# Revit family: Casement_38_B_Side_Hung_Standard
name_source: partatom
category: Windows
revit_build: Autodesk Revit 2014 (Build: 20130308_1515(x64)
units: mm (PartAtom-declared; Revit-internal decimal feet)

## types (18) — shared parameters
Aluminium Thickness = 1 mm  [stored 0.00328084 ft]
Bead SG Gap = 13 mm  [stored 0.0426509 ft]
Casement Dimension = 38 mm  [stored 0.124672 ft]
Custom Sash Width = 554 mm  [stored 1.81759 ft]
DG Extrusion Start = 9 mm  [stored 0.0295276 ft]
DG Gasket Finish = Double Glazing Gasket Material
DG Thickness Calc = 4 mm  [stored 0.0131234 ft]
Default Sill Height = 800 mm  [stored 2.62467 ft]
Depth Bead = 24 mm  [stored 0.0787402 ft]
Description = Window 38mm, Type B side hung
Frame Center Offset = 19 mm  [stored 0.062336 ft]
Limit Fixed Panel Width Max = 1500 mm
Limit Fixed Panel Width Min = 200 mm  [stored 0.656168 ft]
Limit Sash Height Max = 1500 mm
Limit Sash Height Min = 300 mm  [stored 0.984252 ft]
Limit Sash Width Max = 700 mm  [stored 2.29659 ft]
Limit Sash Width Min = 300 mm  [stored 0.984252 ft]
Limit Window Height Max = 1546 mm
Limit Window Height Min = 346 mm
Limit Window Width Max = 2129 mm
Limit Window Width Min = 829 mm  [stored 2.71982 ft]
Manufacturer = Crealco
Max System DG One Piece Thickness = 6 mm  [stored 0.019685 ft]
Max System DG Unit Thickness = 25 mm  [stored 0.082021 ft]
Model = Casement 38
Offset Bead SG Center Reversed = 19 mm  [stored 0.062336 ft]
Offset Mullion Left = 569 mm  [stored 1.8668 ft]
Offset Panel 4 Left = 599 mm  [stored 1.96522 ft]
Offset Sash Left = 23 mm  [stored 0.0754593 ft]
Offset Sash Top = 23 mm  [stored 0.0754593 ft]
Offset Window Exterior = 19 mm  [stored 0.062336 ft]
SG Gasket Thickness = 6 mm  [stored 0.019685 ft]
Sash Center Offset = 16 mm  [stored 0.0524934 ft]
Sash Overlap = 7 mm  [stored 0.0229659 ft]
Sash Spacing Inner = 8 mm  [stored 0.0262467 ft]
URL = http://www.crealco.co.za
Wall Closure = By host
Width Bead = 15 mm  [stored 0.0492126 ft]
Width Panel 1 = 539 mm  [stored 1.76837 ft]
Width Profile = 30 mm  [stored 0.0984252 ft]
Width Sash = 524 mm  [stored 1.71916 ft]
Width Sash Opening = 554 mm  [stored 1.81759 ft]
zero-valued in all types: Window Exterior Offset

## per-type parameters (varying)
- 38-0909S-1000Pa: Area Pane Left=0.37 m²; Area Pane Right=0.21 m²; Clearvue Insulated LowE SHGC Value=0.461; Clearvue Insulated LowE U Value=3.73; Clearvue Insulated SHGC Value=0.505; Clearvue Insulated U Value=4.2; Clearvue U Value=6.25; Custom Windload=1000 mm  [stored 3.28084 ft]; Custom Window Height=890 mm  [stored 2.91995 ft]; Custom Window Width=890 mm  [stored 2.91995 ft]; Depth Mullion=39 mm  [stored 0.127953 ft]; Energy Advantage SHGC Value=0.519; Energy Advantage U Value=4.82; Height=890 mm  [stored 2.91995 ft]; Height Panel 4=830 mm  [stored 2.7231 ft]; Height Sash=814 mm  [stored 2.6706 ft]; Height Sash Opening=844 mm  [stored 2.76903 ft]; Intruderprufe Insulated LowE SHGC Value=0.428; Intruderprufe Insulated LowE U Value=3.69; Intruderprufe Insulated SHGC Value=0.469; Intruderprufe Insulated U Value=4.1; Intruderprufe LowE SHGC Value=0.487; Intruderprufe LowE U Value=4.7; Intruderprufe SHGC Value=0.562; Intruderprufe U Value=6.12; Length Mullion=890 mm  [stored 2.91995 ft]; Max Pane Area=0.37 m²; Mullion Depth Windload Based=39 mm  [stored 0.127953 ft]; Width=890 mm  [stored 2.91995 ft]; Width Panel 4=261 mm  [stored 0.856299 ft]; Windload Design=1000 mm  [stored 3.28084 ft]
- 38-0909S-1500Pa: Area Pane Left=0.37 m²; Area Pane Right=0.21 m²; Clearvue Insulated LowE SHGC Value=0.461; Clearvue Insulated LowE U Value=3.73; Clearvue Insulated SHGC Value=0.505; Clearvue Insulated U Value=4.2; Clearvue U Value=6.25; Custom Windload=1500 mm; Custom Window Height=890 mm  [stored 2.91995 ft]; Custom Window Width=890 mm  [stored 2.91995 ft]; Depth Mullion=39 mm  [stored 0.127953 ft]; Energy Advantage SHGC Value=0.519; Energy Advantage U Value=4.82; Height=890 mm  [stored 2.91995 ft]; Height Panel 4=830 mm  [stored 2.7231 ft]; Height Sash=814 mm  [stored 2.6706 ft]; Height Sash Opening=844 mm  [stored 2.76903 ft]; Intruderprufe Insulated LowE SHGC Value=0.428; Intruderprufe Insulated LowE U Value=3.69; Intruderprufe Insulated SHGC Value=0.469; Intruderprufe Insulated U Value=4.1; Intruderprufe LowE SHGC Value=0.487; Intruderprufe LowE U Value=4.7; Intruderprufe SHGC Value=0.562; Intruderprufe U Value=6.12; Length Mullion=890 mm  [stored 2.91995 ft]; Max Pane Area=0.37 m²; Mullion Depth Windload Based=39 mm  [stored 0.127953 ft]; Width=890 mm  [stored 2.91995 ft]; Width Panel 4=261 mm  [stored 0.856299 ft]; Windload Design=1500 mm
- 38-0909S-2000Pa: Area Pane Left=0.37 m²; Area Pane Right=0.21 m²; Clearvue Insulated LowE SHGC Value=0.461; Clearvue Insulated LowE U Value=3.73; Clearvue Insulated SHGC Value=0.505; Clearvue Insulated U Value=4.2; Clearvue U Value=6.25; Custom Windload=2000 mm; Custom Window Height=890 mm  [stored 2.91995 ft]; Custom Window Width=890 mm  [stored 2.91995 ft]; Depth Mullion=39 mm  [stored 0.127953 ft]; Energy Advantage SHGC Value=0.519; Energy Advantage U Value=4.82; Height=890 mm  [stored 2.91995 ft]; Height Panel 4=830 mm  [stored 2.7231 ft]; Height Sash=814 mm  [stored 2.6706 ft]; Height Sash Opening=844 mm  [stored 2.76903 ft]; Intruderprufe Insulated LowE SHGC Value=0.428; Intruderprufe Insulated LowE U Value=3.69; Intruderprufe Insulated SHGC Value=0.469; Intruderprufe Insulated U Value=4.1; Intruderprufe LowE SHGC Value=0.487; Intruderprufe LowE U Value=4.7; Intruderprufe SHGC Value=0.562; Intruderprufe U Value=6.12; Length Mullion=890 mm  [stored 2.91995 ft]; Max Pane Area=0.37 m²; Mullion Depth Windload Based=39 mm  [stored 0.127953 ft]; Width=890 mm  [stored 2.91995 ft]; Width Panel 4=261 mm  [stored 0.856299 ft]; Windload Design=2000 mm
- 38-1209S-1000Pa: Area Pane Left=0.37 m²; Area Pane Right=0.45 m²; Clearvue Insulated LowE SHGC Value=0.498; Clearvue Insulated LowE U Value=3.42; Clearvue Insulated SHGC Value=0.547; Clearvue Insulated U Value=3.95; Clearvue U Value=6.18; Custom Windload=1000 mm  [stored 3.28084 ft]; Custom Window Height=890 mm  [stored 2.91995 ft]; Custom Window Width=1190 mm; Depth Mullion=39 mm  [stored 0.127953 ft]; Energy Advantage SHGC Value=0.56; Energy Advantage U Value=4.63; Height=890 mm  [stored 2.91995 ft]; Height Panel 4=830 mm  [stored 2.7231 ft]; Height Sash=814 mm  [stored 2.6706 ft]; Height Sash Opening=844 mm  [stored 2.76903 ft]; Intruderprufe Insulated LowE SHGC Value=0.462; Intruderprufe Insulated LowE U Value=3.35; Intruderprufe Insulated SHGC Value=0.507; Intruderprufe Insulated U Value=3.85; Intruderprufe LowE SHGC Value=0.525; Intruderprufe LowE U Value=4.51; Intruderprufe SHGC Value=0.602; Intruderprufe U Value=6.05; Length Mullion=890 mm  [stored 2.91995 ft]; Max Pane Area=0.45 m²; Mullion Depth Windload Based=39 mm  [stored 0.127953 ft]; Width=1190 mm; Width Panel 4=561 mm; Windload Design=1000 mm  [stored 3.28084 ft]
- 38-1209S-1500Pa: Area Pane Left=0.37 m²; Area Pane Right=0.45 m²; Clearvue Insulated LowE SHGC Value=0.498; Clearvue Insulated LowE U Value=3.42; Clearvue Insulated SHGC Value=0.547; Clearvue Insulated U Value=3.95; Clearvue U Value=6.18; Custom Windload=1500 mm; Custom Window Height=890 mm  [stored 2.91995 ft]; Custom Window Width=1190 mm; Depth Mullion=39 mm  [stored 0.127953 ft]; Energy Advantage SHGC Value=0.56; Energy Advantage U Value=4.63; Height=890 mm  [stored 2.91995 ft]; Height Panel 4=830 mm  [stored 2.7231 ft]; Height Sash=814 mm  [stored 2.6706 ft]; Height Sash Opening=844 mm  [stored 2.76903 ft]; Intruderprufe Insulated LowE SHGC Value=0.462; Intruderprufe Insulated LowE U Value=3.35; Intruderprufe Insulated SHGC Value=0.507; Intruderprufe Insulated U Value=3.85; Intruderprufe LowE SHGC Value=0.525; Intruderprufe LowE U Value=4.51; Intruderprufe SHGC Value=0.602; Intruderprufe U Value=6.05; Length Mullion=890 mm  [stored 2.91995 ft]; Max Pane Area=0.45 m²; Mullion Depth Windload Based=39 mm  [stored 0.127953 ft]; Width=1190 mm; Width Panel 4=561 mm; Windload Design=1500 mm
- 38-1209S-2000Pa: Area Pane Left=0.37 m²; Area Pane Right=0.45 m²; Clearvue Insulated LowE SHGC Value=0.498; Clearvue Insulated LowE U Value=3.42; Clearvue Insulated SHGC Value=0.547; Clearvue Insulated U Value=3.95; Clearvue U Value=6.18; Custom Windload=2000 mm; Custom Window Height=890 mm  [stored 2.91995 ft]; Custom Window Width=1190 mm; Depth Mullion=39 mm  [stored 0.127953 ft]; Energy Advantage SHGC Value=0.56; Energy Advantage U Value=4.63; Height=890 mm  [stored 2.91995 ft]; Height Panel 4=830 mm  [stored 2.7231 ft]; Height Sash=814 mm  [stored 2.6706 ft]; Height Sash Opening=844 mm  [stored 2.76903 ft]; Intruderprufe Insulated LowE SHGC Value=0.462; Intruderprufe Insulated LowE U Value=3.35; Intruderprufe Insulated SHGC Value=0.507; Intruderprufe Insulated U Value=3.85; Intruderprufe LowE SHGC Value=0.525; Intruderprufe LowE U Value=4.51; Intruderprufe SHGC Value=0.602; Intruderprufe U Value=6.05; Length Mullion=890 mm  [stored 2.91995 ft]; Max Pane Area=0.45 m²; Mullion Depth Windload Based=39 mm  [stored 0.127953 ft]; Width=1190 mm; Width Panel 4=561 mm; Windload Design=2000 mm
- 38-1509S-1000Pa: Area Pane Left=0.37 m²; Area Pane Right=0.7 m²; Clearvue Insulated LowE SHGC Value=0.521; Clearvue Insulated LowE U Value=3.24; Clearvue Insulated SHGC Value=0.572; Clearvue Insulated U Value=3.8; Clearvue U Value=6.13; Custom Windload=1000 mm  [stored 3.28084 ft]; Custom Window Height=890 mm  [stored 2.91995 ft]; Custom Window Width=1490 mm; Depth Mullion=39 mm  [stored 0.127953 ft]; Energy Advantage SHGC Value=0.585; Energy Advantage U Value=4.51; Height=890 mm  [stored 2.91995 ft]; Height Panel 4=830 mm  [stored 2.7231 ft]; Height Sash=814 mm  [stored 2.6706 ft]; Height Sash Opening=844 mm  [stored 2.76903 ft]; Intruderprufe Insulated LowE SHGC Value=0.482; Intruderprufe Insulated LowE U Value=3.17; Intruderprufe Insulated SHGC Value=0.53; Intruderprufe Insulated U Value=3.71; Intruderprufe LowE SHGC Value=0.547; Intruderprufe LowE U Value=4.4; Intruderprufe SHGC Value=0.626; Intruderprufe U Value=6.01; Length Mullion=890 mm  [stored 2.91995 ft]; Max Pane Area=0.7 m²; Mullion Depth Windload Based=39 mm  [stored 0.127953 ft]; Width=1490 mm; Width Panel 4=861 mm; Windload Design=1000 mm  [stored 3.28084 ft]
- 38-1509S-1500Pa: Area Pane Left=0.37 m²; Area Pane Right=0.7 m²; Clearvue Insulated LowE SHGC Value=0.521; Clearvue Insulated LowE U Value=3.24; Clearvue Insulated SHGC Value=0.572; Clearvue Insulated U Value=3.8; Clearvue U Value=6.13; Custom Windload=1500 mm; Custom Window Height=890 mm  [stored 2.91995 ft]; Custom Window Width=1490 mm; Depth Mullion=39 mm  [stored 0.127953 ft]; Energy Advantage SHGC Value=0.585; Energy Advantage U Value=4.51; Height=890 mm  [stored 2.91995 ft]; Height Panel 4=830 mm  [stored 2.7231 ft]; Height Sash=814 mm  [stored 2.6706 ft]; Height Sash Opening=844 mm  [stored 2.76903 ft]; Intruderprufe Insulated LowE SHGC Value=0.482; Intruderprufe Insulated LowE U Value=3.17; Intruderprufe Insulated SHGC Value=0.53; Intruderprufe Insulated U Value=3.71; Intruderprufe LowE SHGC Value=0.547; Intruderprufe LowE U Value=4.4; Intruderprufe SHGC Value=0.626; Intruderprufe U Value=6.01; Length Mullion=890 mm  [stored 2.91995 ft]; Max Pane Area=0.7 m²; Mullion Depth Windload Based=39 mm  [stored 0.127953 ft]; Width=1490 mm; Width Panel 4=861 mm; Windload Design=1500 mm
- 38-1509S-2000Pa: Area Pane Left=0.37 m²; Area Pane Right=0.7 m²; Clearvue Insulated LowE SHGC Value=0.521; Clearvue Insulated LowE U Value=3.24; Clearvue Insulated SHGC Value=0.572; Clearvue Insulated U Value=3.8; Clearvue U Value=6.13; Custom Windload=2000 mm; Custom Window Height=890 mm  [stored 2.91995 ft]; Custom Window Width=1490 mm; Depth Mullion=39 mm  [stored 0.127953 ft]; Energy Advantage SHGC Value=0.585; Energy Advantage U Value=4.51; Height=890 mm  [stored 2.91995 ft]; Height Panel 4=830 mm  [stored 2.7231 ft]; Height Sash=814 mm  [stored 2.6706 ft]; Height Sash Opening=844 mm  [stored 2.76903 ft]; Intruderprufe Insulated LowE SHGC Value=0.482; Intruderprufe Insulated LowE U Value=3.17; Intruderprufe Insulated SHGC Value=0.53; Intruderprufe Insulated U Value=3.71; Intruderprufe LowE SHGC Value=0.547; Intruderprufe LowE U Value=4.4; Intruderprufe SHGC Value=0.626; Intruderprufe U Value=6.01; Length Mullion=890 mm  [stored 2.91995 ft]; Max Pane Area=0.7 m²; Mullion Depth Windload Based=39 mm  [stored 0.127953 ft]; Width=1490 mm; Width Panel 4=861 mm; Windload Design=2000 mm
- 38-0912S-1000Pa: Area Pane Left=0.52 m²; Area Pane Right=0.28 m²; Clearvue Insulated LowE SHGC Value=0.478; Clearvue Insulated LowE U Value=3.6; Clearvue Insulated SHGC Value=0.525; Clearvue Insulated U Value=4.09; Clearvue U Value=6.23; Custom Windload=1000 mm  [stored 3.28084 ft]; Custom Window Height=1190 mm; Custom Window Width=890 mm  [stored 2.91995 ft]; Depth Mullion=39 mm  [stored 0.127953 ft]; Energy Advantage SHGC Value=0.539; Energy Advantage U Value=4.47; Height=1190 mm; Height Panel 4=1130 mm  [stored 3.70735 ft]; Height Sash=1114 mm  [stored 3.65486 ft]; Height Sash Opening=1144 mm; Intruderprufe Insulated LowE SHGC Value=0.444; Intruderprufe Insulated LowE U Value=3.52; Intruderprufe Insulated SHGC Value=0.487; Intruderprufe Insulated U Value=3.99; Intruderprufe LowE SHGC Value=0.504; Intruderprufe LowE U Value=4.64; Intruderprufe SHGC Value=0.584; Intruderprufe U Value=6.1; Length Mullion=1190 mm; Max Pane Area=0.52 m²; Mullion Depth Windload Based=39 mm  [stored 0.127953 ft]; Width=890 mm  [stored 2.91995 ft]; Width Panel 4=261 mm  [stored 0.856299 ft]; Windload Design=1000 mm  [stored 3.28084 ft]
- 38-0912S-1500Pa: Area Pane Left=0.52 m²; Area Pane Right=0.28 m²; Clearvue Insulated LowE SHGC Value=0.478; Clearvue Insulated LowE U Value=3.6; Clearvue Insulated SHGC Value=0.525; Clearvue Insulated U Value=4.09; Clearvue U Value=6.23; Custom Windload=1500 mm; Custom Window Height=1190 mm; Custom Window Width=890 mm  [stored 2.91995 ft]; Depth Mullion=39 mm  [stored 0.127953 ft]; Energy Advantage SHGC Value=0.539; Energy Advantage U Value=4.47; Height=1190 mm; Height Panel 4=1130 mm  [stored 3.70735 ft]; Height Sash=1114 mm  [stored 3.65486 ft]; Height Sash Opening=1144 mm; Intruderprufe Insulated LowE SHGC Value=0.444; Intruderprufe Insulated LowE U Value=3.52; Intruderprufe Insulated SHGC Value=0.487; Intruderprufe Insulated U Value=3.99; Intruderprufe LowE SHGC Value=0.504; Intruderprufe LowE U Value=4.64; Intruderprufe SHGC Value=0.584; Intruderprufe U Value=6.1; Length Mullion=1190 mm; Max Pane Area=0.52 m²; Mullion Depth Windload Based=39 mm  [stored 0.127953 ft]; Width=890 mm  [stored 2.91995 ft]; Width Panel 4=261 mm  [stored 0.856299 ft]; Windload Design=1500 mm
- 38-0912S-2000Pa: Area Pane Left=0.52 m²; Area Pane Right=0.28 m²; Clearvue Insulated LowE SHGC Value=0.478; Clearvue Insulated LowE U Value=3.6; Clearvue Insulated SHGC Value=0.525; Clearvue Insulated U Value=4.09; Clearvue U Value=6.23; Custom Windload=2000 mm; Custom Window Height=1190 mm; Custom Window Width=890 mm  [stored 2.91995 ft]; Depth Mullion=39 mm  [stored 0.127953 ft]; Energy Advantage SHGC Value=0.539; Energy Advantage U Value=4.47; Height=1190 mm; Height Panel 4=1130 mm  [stored 3.70735 ft]; Height Sash=1114 mm  [stored 3.65486 ft]; Height Sash Opening=1144 mm; Intruderprufe Insulated LowE SHGC Value=0.444; Intruderprufe Insulated LowE U Value=3.52; Intruderprufe Insulated SHGC Value=0.487; Intruderprufe Insulated U Value=3.99; Intruderprufe LowE SHGC Value=0.504; Intruderprufe LowE U Value=4.64; Intruderprufe SHGC Value=0.584; Intruderprufe U Value=6.1; Length Mullion=1190 mm; Max Pane Area=0.52 m²; Mullion Depth Windload Based=39 mm  [stored 0.127953 ft]; Width=890 mm  [stored 2.91995 ft]; Width Panel 4=261 mm  [stored 0.856299 ft]; Windload Design=2000 mm
- 38-1212S-1000Pa: Area Pane Left=0.52 m²; Area Pane Right=0.62 m²; Clearvue Insulated LowE SHGC Value=0.516; Clearvue Insulated LowE U Value=3.29; Clearvue Insulated SHGC Value=0.567; Clearvue Insulated U Value=3.84; Clearvue U Value=6.16; Custom Windload=1000 mm  [stored 3.28084 ft]; Custom Window Height=1190 mm; Custom Window Width=1190 mm; Depth Mullion=39 mm  [stored 0.127953 ft]; Energy Advantage SHGC Value=0.58; Energy Advantage U Value=4.54; Height=1190 mm; Height Panel 4=1130 mm  [stored 3.70735 ft]; Height Sash=1114 mm  [stored 3.65486 ft]; Height Sash Opening=1144 mm; Intruderprufe Insulated LowE SHGC Value=0.477; Intruderprufe Insulated LowE U Value=3.21; Intruderprufe Insulated SHGC Value=0.525; Intruderprufe Insulated U Value=3.75; Intruderprufe LowE SHGC Value=0.542; Intruderprufe LowE U Value=4.43; Intruderprufe SHGC Value=0.623; Intruderprufe U Value=6.03; Length Mullion=1190 mm; Max Pane Area=0.62 m²; Mullion Depth Windload Based=39 mm  [stored 0.127953 ft]; Width=1190 mm; Width Panel 4=561 mm; Windload Design=1000 mm  [stored 3.28084 ft]
- 38-1212S-1500Pa: Area Pane Left=0.52 m²; Area Pane Right=0.62 m²; Clearvue Insulated LowE SHGC Value=0.516; Clearvue Insulated LowE U Value=3.29; Clearvue Insulated SHGC Value=0.567; Clearvue Insulated U Value=3.84; Clearvue U Value=6.16; Custom Windload=1500 mm; Custom Window Height=1190 mm; Custom Window Width=1190 mm; Depth Mullion=39 mm  [stored 0.127953 ft]; Energy Advantage SHGC Value=0.58; Energy Advantage U Value=4.54; Height=1190 mm; Height Panel 4=1130 mm  [stored 3.70735 ft]; Height Sash=1114 mm  [stored 3.65486 ft]; Height Sash Opening=1144 mm; Intruderprufe Insulated LowE SHGC Value=0.477; Intruderprufe Insulated LowE U Value=3.21; Intruderprufe Insulated SHGC Value=0.525; Intruderprufe Insulated U Value=3.75; Intruderprufe LowE SHGC Value=0.542; Intruderprufe LowE U Value=4.43; Intruderprufe SHGC Value=0.623; Intruderprufe U Value=6.03; Length Mullion=1190 mm; Max Pane Area=0.62 m²; Mullion Depth Windload Based=39 mm  [stored 0.127953 ft]; Width=1190 mm; Width Panel 4=561 mm; Windload Design=1500 mm
- 38-1212S-2000Pa: Area Pane Left=0.52 m²; Area Pane Right=0.62 m²; Clearvue Insulated LowE SHGC Value=0.516; Clearvue Insulated LowE U Value=3.29; Clearvue Insulated SHGC Value=0.567; Clearvue Insulated U Value=3.84; Clearvue U Value=6.16; Custom Windload=2000 mm; Custom Window Height=1190 mm; Custom Window Width=1190 mm; Depth Mullion=39 mm  [stored 0.127953 ft]; Energy Advantage SHGC Value=0.58; Energy Advantage U Value=4.54; Height=1190 mm; Height Panel 4=1130 mm  [stored 3.70735 ft]; Height Sash=1114 mm  [stored 3.65486 ft]; Height Sash Opening=1144 mm; Intruderprufe Insulated LowE SHGC Value=0.477; Intruderprufe Insulated LowE U Value=3.21; Intruderprufe Insulated SHGC Value=0.525; Intruderprufe Insulated U Value=3.75; Intruderprufe LowE SHGC Value=0.542; Intruderprufe LowE U Value=4.43; Intruderprufe SHGC Value=0.623; Intruderprufe U Value=6.03; Length Mullion=1190 mm; Max Pane Area=0.62 m²; Mullion Depth Windload Based=39 mm  [stored 0.127953 ft]; Width=1190 mm; Width Panel 4=561 mm; Windload Design=2000 mm
- 38-1512S-1000Pa: Area Pane Left=0.52 m²; Area Pane Right=0.95 m²; Clearvue Insulated LowE SHGC Value=0.538; Clearvue Insulated LowE U Value=3.1; Clearvue Insulated SHGC Value=0.592; Clearvue Insulated U Value=3.69; Clearvue U Value=6.11; Custom Windload=1000 mm  [stored 3.28084 ft]; Custom Window Height=1190 mm; Custom Window Width=1490 mm; Depth Mullion=39 mm  [stored 0.127953 ft]; Energy Advantage SHGC Value=0.604; Energy Advantage U Value=4.42; Height=1190 mm; Height Panel 4=1130 mm  [stored 3.70735 ft]; Height Sash=1114 mm  [stored 3.65486 ft]; Height Sash Opening=1144 mm; Intruderprufe Insulated LowE SHGC Value=0.497; Intruderprufe Insulated LowE U Value=3.03; Intruderprufe Insulated SHGC Value=0.548; Intruderprufe Insulated U Value=3.6; Intruderprufe LowE SHGC Value=0.565; Intruderprufe LowE U Value=4.32; Intruderprufe SHGC Value=0.647; Intruderprufe U Value=5.99; Length Mullion=1190 mm; Max Pane Area=0.95 m²; Mullion Depth Windload Based=39 mm  [stored 0.127953 ft]; Width=1490 mm; Width Panel 4=861 mm; Windload Design=1000 mm  [stored 3.28084 ft]
- 38-1512S-1500Pa: Area Pane Left=0.52 m²; Area Pane Right=0.95 m²; Clearvue Insulated LowE SHGC Value=0.538; Clearvue Insulated LowE U Value=3.1; Clearvue Insulated SHGC Value=0.592; Clearvue Insulated U Value=3.69; Clearvue U Value=6.11; Custom Windload=1500 mm; Custom Window Height=1190 mm; Custom Window Width=1490 mm; Depth Mullion=39 mm  [stored 0.127953 ft]; Energy Advantage SHGC Value=0.604; Energy Advantage U Value=4.42; Height=1190 mm; Height Panel 4=1130 mm  [stored 3.70735 ft]; Height Sash=1114 mm  [stored 3.65486 ft]; Height Sash Opening=1144 mm; Intruderprufe Insulated LowE SHGC Value=0.497; Intruderprufe Insulated LowE U Value=3.03; Intruderprufe Insulated SHGC Value=0.548; Intruderprufe Insulated U Value=3.6; Intruderprufe LowE SHGC Value=0.565; Intruderprufe LowE U Value=4.32; Intruderprufe SHGC Value=0.647; Intruderprufe U Value=5.99; Length Mullion=1190 mm; Max Pane Area=0.95 m²; Mullion Depth Windload Based=39 mm  [stored 0.127953 ft]; Width=1490 mm; Width Panel 4=861 mm; Windload Design=1500 mm
- 38-1512S-2000Pa: Area Pane Left=0.52 m²; Area Pane Right=0.95 m²; Clearvue Insulated LowE SHGC Value=0.539; Clearvue Insulated LowE U Value=3.14; Clearvue Insulated SHGC Value=0.592; Clearvue Insulated U Value=3.73; Clearvue U Value=6.11; Custom Windload=2000 mm; Custom Window Height=1190 mm; Custom Window Width=1490 mm; Depth Mullion=54 mm  [stored 0.177165 ft]; Energy Advantage SHGC Value=0.603; Energy Advantage U Value=4.48; Height=1190 mm; Height Panel 4=1130 mm  [stored 3.70735 ft]; Height Sash=1114 mm  [stored 3.65486 ft]; Height Sash Opening=1144 mm; Intruderprufe Insulated LowE SHGC Value=0.499; Intruderprufe Insulated LowE U Value=3.08; Intruderprufe Insulated SHGC Value=0.55; Intruderprufe Insulated U Value=3.64; Intruderprufe LowE SHGC Value=0.566; Intruderprufe LowE U Value=4.37; Intruderprufe SHGC Value=0.636; Intruderprufe U Value=6; Length Mullion=1190 mm; Max Pane Area=0.95 m²; Mullion Depth Windload Based=54 mm  [stored 0.177165 ft]; Width=1490 mm; Width Panel 4=861 mm; Windload Design=2000 mm

note: [stored X ft] marks values corroborated as IEEE doubles in the binary element streams (Revit-internal decimal feet)

## geometry (parser evidence)
native form markers: Extrusion x1, Sweep x28
no freeform markers — native parametric forms only
